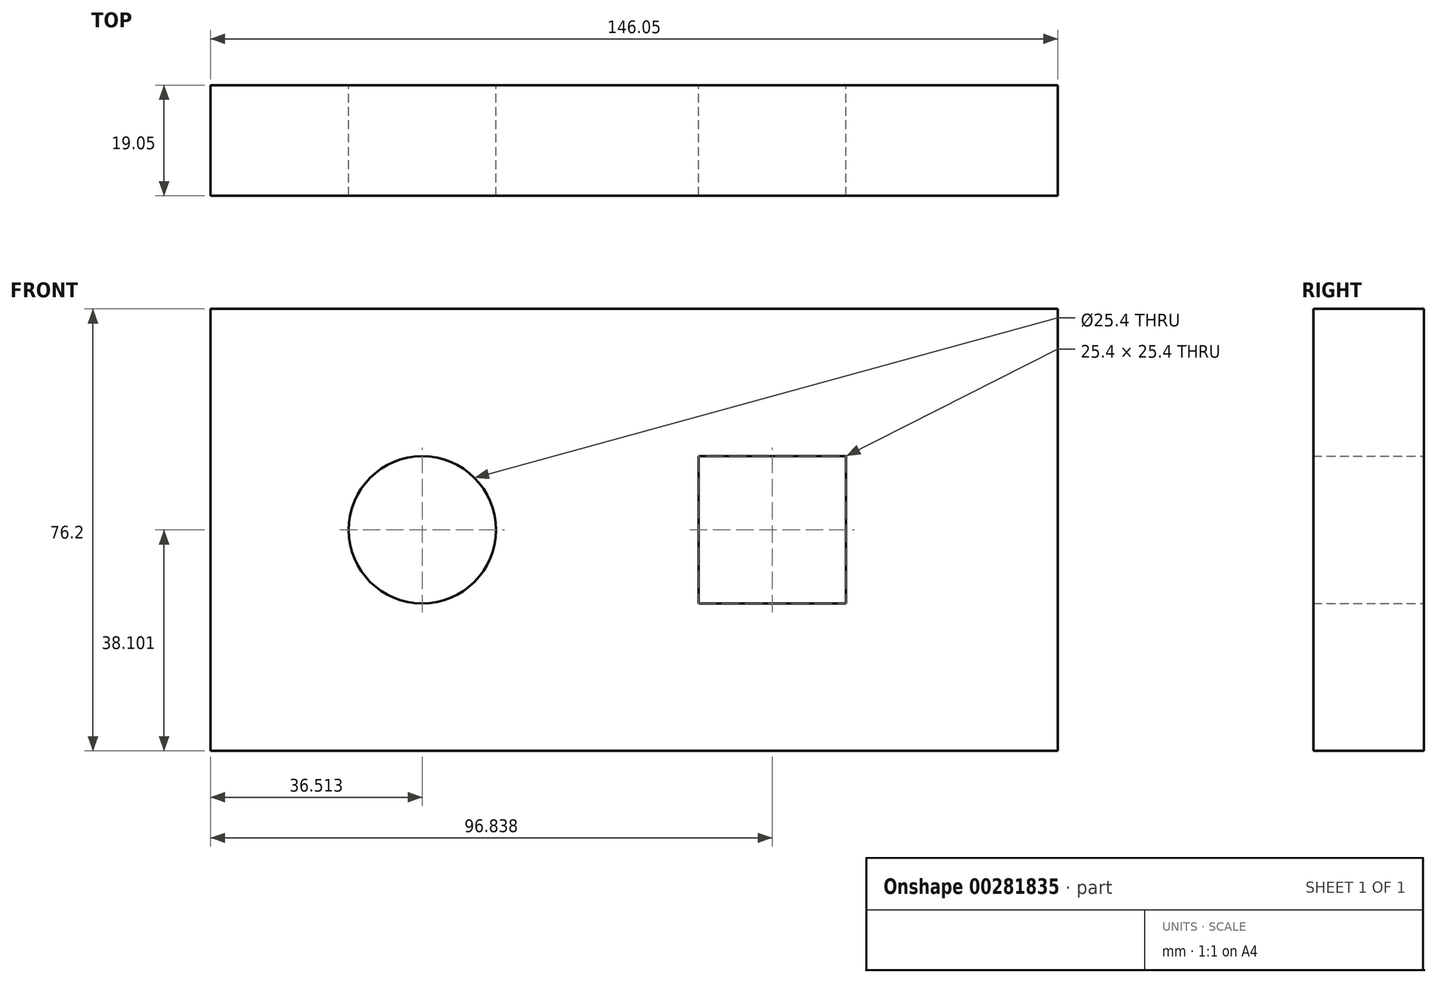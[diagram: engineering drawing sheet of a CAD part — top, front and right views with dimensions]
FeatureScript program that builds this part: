
annotation { "Feature Type Name" : "Feature", "Feature Type Description" : "" }
export const myFeature = defineFeature(function(context is Context, id is Id, definition is map)
    precondition{}
    {
        {
            var Q0;
            Q0=qCreatedBy(makeId("Front.planeOp"),FACE);
            var sketch = newSketch(context, id + "F0", { "sketchPlane" : qUnion([Q0])});
            skLineSegment(sketch, "E0.bottom", {"start": v(117.71, -19.34) * mm, "end": v(-28.34, -19.34) * mm});
            skLineSegment(sketch, "E0.top", {"start": v(117.71, 56.86) * mm, "end": v(-28.34, 56.86) * mm});
            skLineSegment(sketch, "E0.left", {"start": v(117.71, -19.34) * mm, "end": v(117.71, 56.86) * mm});
            skLineSegment(sketch, "E0.right", {"start": v(-28.34, -19.34) * mm, "end": v(-28.34, 56.86) * mm});
            skCircle(sketch, "E1", {"center": v(8.17, 18.76) * mm, "radius": 12.7 * mm});
            skLineSegment(sketch, "E2.bottom", {"start": v(81.2, 6.06) * mm, "end": v(55.8, 6.06) * mm});
            skLineSegment(sketch, "E2.top", {"start": v(81.2, 31.46) * mm, "end": v(55.8, 31.46) * mm});
            skLineSegment(sketch, "E2.left", {"start": v(81.2, 6.06) * mm, "end": v(81.2, 31.46) * mm});
            skLineSegment(sketch, "E2.right", {"start": v(55.8, 6.06) * mm, "end": v(55.8, 31.46) * mm});
            skSolve(sketch);
        }
        {
            var Q0;
            Q0 = qSketchRegion(id + "F0", true);
            extrude(context, id + "F1", {"entities" : qUnion([Q0]), "depth" : 19.05 * mm});
        }
    });
